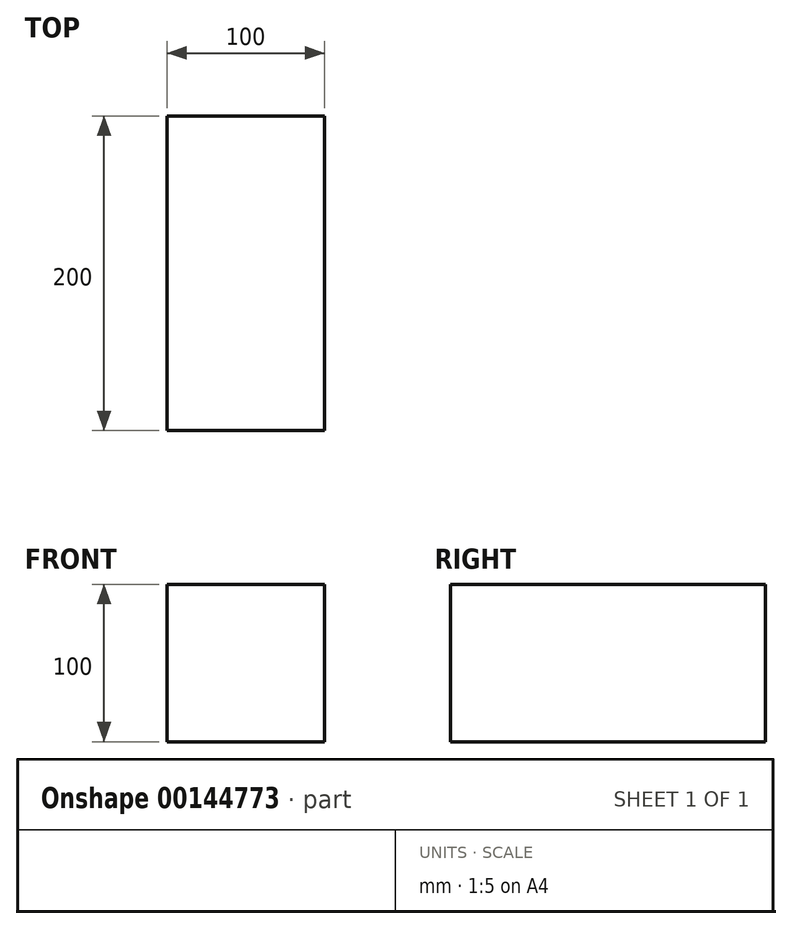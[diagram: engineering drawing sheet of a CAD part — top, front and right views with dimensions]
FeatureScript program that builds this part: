
annotation { "Feature Type Name" : "Feature", "Feature Type Description" : "" }
export const myFeature = defineFeature(function(context is Context, id is Id, definition is map)
    precondition{}
    {
        {
            var Q0;
            Q0=qCreatedBy(makeId("Top.planeOp"),FACE);
            var sketch = newSketch(context, id + "F0", { "sketchPlane" : qUnion([Q0])});
            skLineSegment(sketch, "E0.bottom", {"start": v(50, 100) * mm, "end": v(-50, 100) * mm});
            skLineSegment(sketch, "E0.top", {"start": v(50, -100) * mm, "end": v(-50, -100) * mm});
            skLineSegment(sketch, "E0.left", {"start": v(50, 100) * mm, "end": v(50, -100) * mm});
            skLineSegment(sketch, "E0.right", {"start": v(-50, 100) * mm, "end": v(-50, -100) * mm});
            skPoint(sketch, "E0.middle", {"position": v(0, 0) * mm});
            skSolve(sketch);
        }
        {
            var Q0;
            Q0=makeQuery(id+"F0.imprint","IMPRINT",FACE,{"disambiguationData":[TD([[makeQuery(id+"F0.imprint","IMPRINT",EDGE,{"derivedFrom":sQuery(id+"F0.wireOp",EDGE,"E0.bottom")}),1.0]])]});
            extrude(context, id + "F1", {"entities" : qUnion([Q0]), "depth" : 100 * mm});
        }
    });
